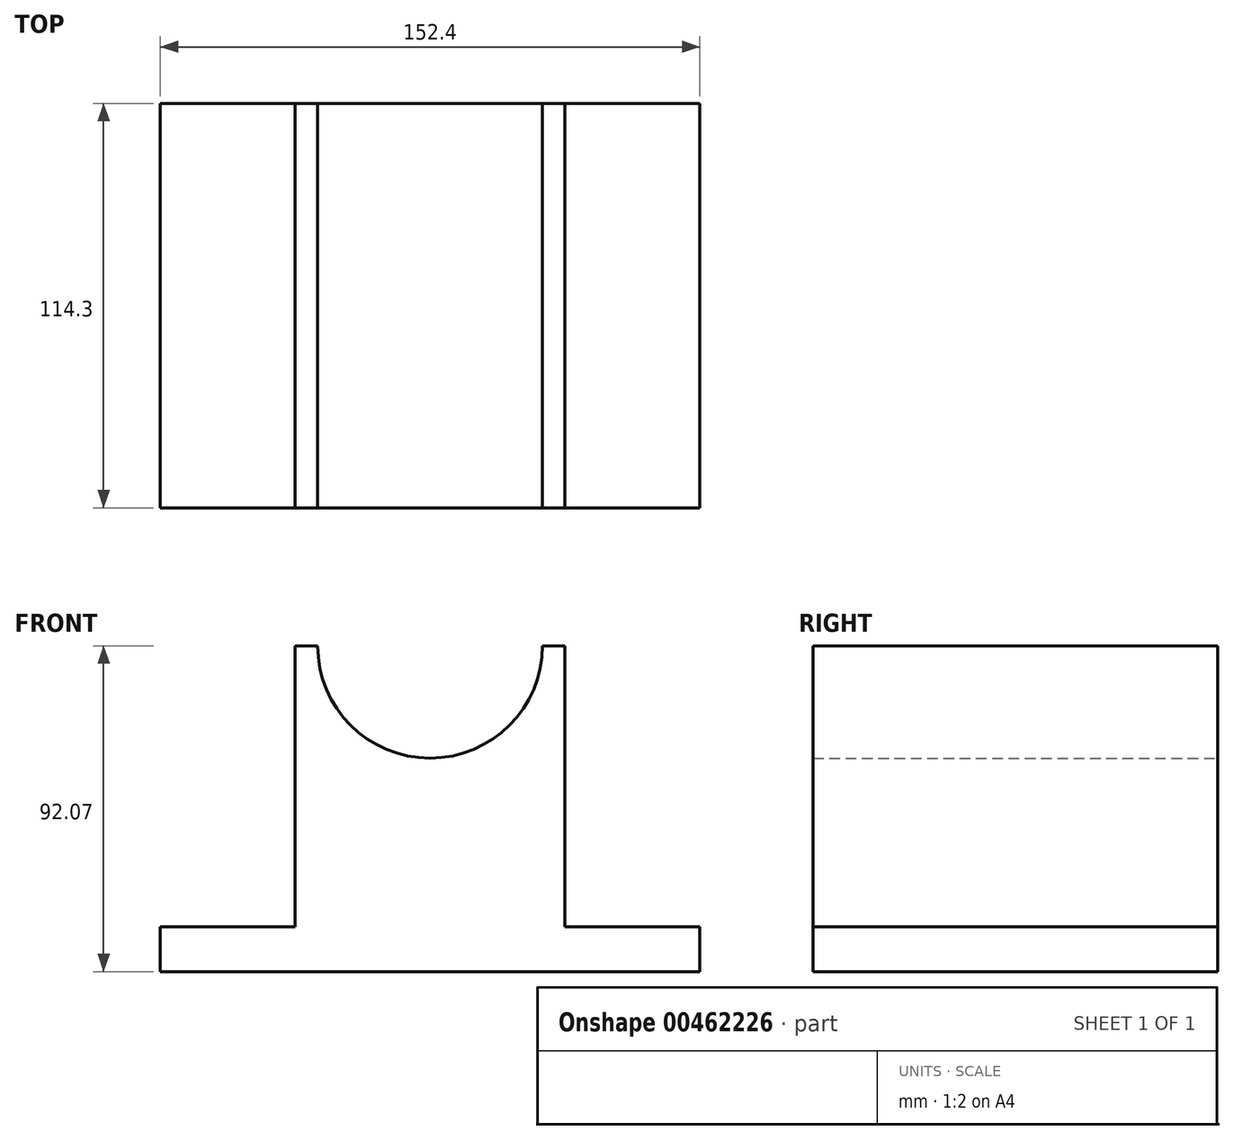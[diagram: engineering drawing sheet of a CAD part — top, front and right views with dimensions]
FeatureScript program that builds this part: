
annotation { "Feature Type Name" : "Feature", "Feature Type Description" : "" }
export const myFeature = defineFeature(function(context is Context, id is Id, definition is map)
    precondition{}
    {
        {
            var Q0;
            Q0=qCreatedBy(makeId("Front.planeOp"),FACE);
            var sketch = newSketch(context, id + "F0", { "sketchPlane" : qUnion([Q0])});
            skLineSegment(sketch, "E0", {"start": v(38.1, 31.9) * mm, "end": v(31.75, 31.9) * mm});
            skLineSegment(sketch, "E1.MirrorCS", {"start": v(-38.1, -47.47) * mm, "end": v(-38.1, 33.03) * mm});
            skLineSegment(sketch, "E2.MirrorCS", {"start": v(-38.1, 31.9) * mm, "end": v(-31.75, 31.9) * mm});
            skLineSegment(sketch, "E3.MirrorCS", {"start": v(-76.2, -47.47) * mm, "end": v(-38.1, -47.47) * mm});
            skLineSegment(sketch, "E4.MirrorCS", {"start": v(-76.2, -60.17) * mm, "end": v(-76.2, -47.47) * mm});
            skLineSegment(sketch, "E5", {"start": v(-76.2, -60.17) * mm, "end": v(76.2, -60.17) * mm});
            skArc(sketch, "E6", {"start": v(-31.75, 31.9) * mm, "mid": v(0, 0.15) * mm, "end": v(31.75, 31.9) * mm});
            skLineSegment(sketch, "E7", {"start": v(0, 47.41) * mm, "end": v(0, -143.7) * mm, "construction": true});
            skLineSegment(sketch, "E8.MirrorCS", {"start": v(76.2, -47.47) * mm, "end": v(38.1, -47.47) * mm});
            skLineSegment(sketch, "E9.MirrorCS", {"start": v(76.2, -60.17) * mm, "end": v(76.2, -47.47) * mm});
            skLineSegment(sketch, "E10.MirrorCS", {"start": v(76.2, -60.17) * mm, "end": v(-76.2, -60.17) * mm});
            skLineSegment(sketch, "E11.MirrorCS", {"start": v(38.1, -47.47) * mm, "end": v(38.1, 33.03) * mm});
            skSolve(sketch);
        }
        {
            var Q0;
            Q0 = qSketchRegion(id + "F0", true);
            extrude(context, id + "F1", {"entities" : qUnion([Q0]), "depth" : 114.3 * mm});
        }
    });
